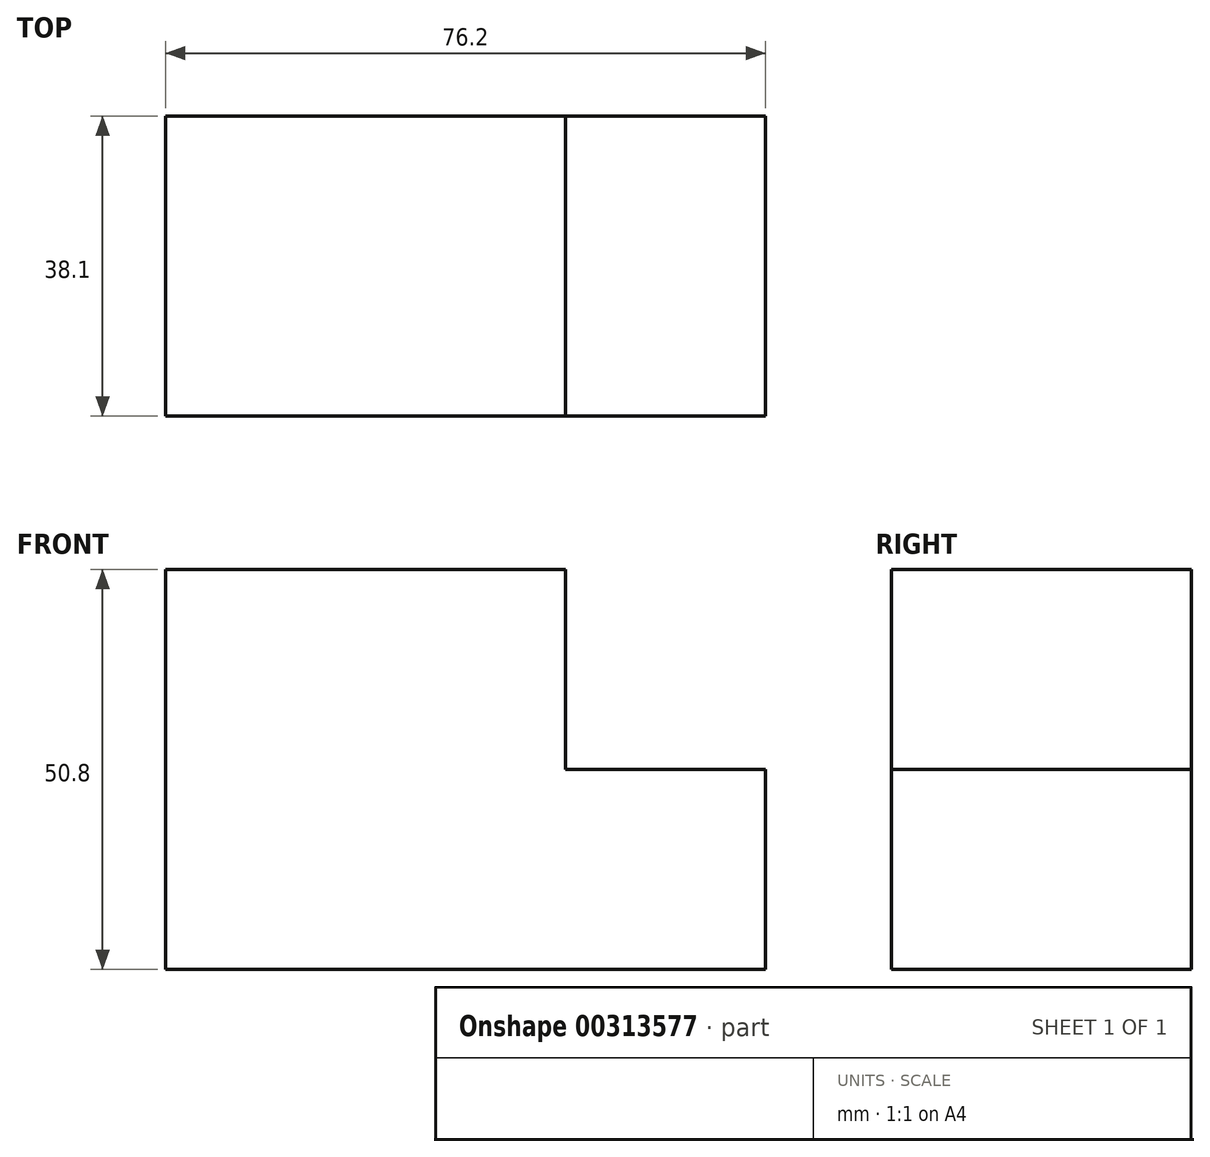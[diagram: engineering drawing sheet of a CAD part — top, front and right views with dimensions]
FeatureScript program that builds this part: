
annotation { "Feature Type Name" : "Feature", "Feature Type Description" : "" }
export const myFeature = defineFeature(function(context is Context, id is Id, definition is map)
    precondition{}
    {
        {
            var Q0;
            Q0=qCreatedBy(makeId("Front.planeOp"),FACE);
            var sketch = newSketch(context, id + "F0", { "sketchPlane" : qUnion([Q0])});
            skLineSegment(sketch, "E0", {"start": v(-32.54, -38.4) * mm, "end": v(43.66, -38.4) * mm});
            skLineSegment(sketch, "E1", {"start": v(43.66, -38.4) * mm, "end": v(43.66, -13) * mm});
            skLineSegment(sketch, "E2", {"start": v(43.66, -13) * mm, "end": v(18.26, -13) * mm});
            skLineSegment(sketch, "E3", {"start": v(18.26, -13) * mm, "end": v(18.26, 12.4) * mm});
            skLineSegment(sketch, "E4", {"start": v(18.26, 12.4) * mm, "end": v(-32.54, 12.4) * mm});
            skLineSegment(sketch, "E5", {"start": v(-32.54, 12.4) * mm, "end": v(-32.54, -38.4) * mm});
            skSolve(sketch);
        }
        {
            var Q0;
            Q0=makeQuery(id+"F0.imprint","IMPRINT",FACE,{"disambiguationData":[TD([[makeQuery(id+"F0.imprint","IMPRINT",EDGE,{"derivedFrom":sQuery(id+"F0.wireOp",EDGE,"E0")}),1.0]])]});
            extrude(context, id + "F1", {"entities" : qUnion([Q0]), "depth" : 38.1 * mm});
        }
    });
